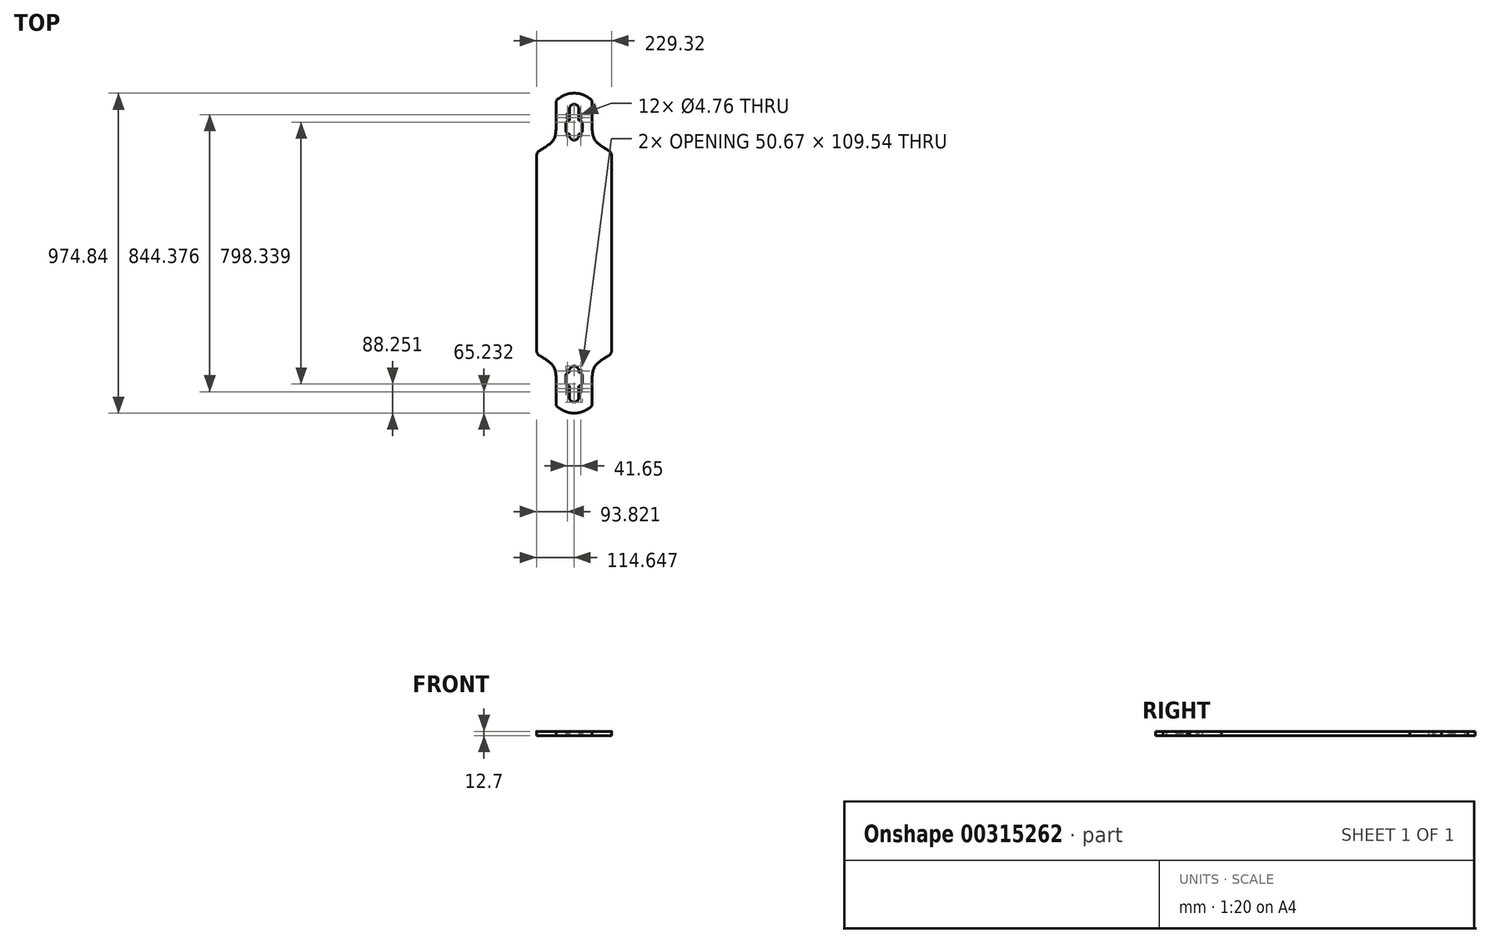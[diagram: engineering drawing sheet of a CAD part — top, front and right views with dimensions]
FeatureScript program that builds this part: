
annotation { "Feature Type Name" : "Feature", "Feature Type Description" : "" }
export const myFeature = defineFeature(function(context is Context, id is Id, definition is map)
    precondition{}
    {
        {
            var Q0;
            Q0=qCreatedBy(makeId("Top.planeOp"),FACE);
            var sketch = newSketch(context, id + "F0", { "sketchPlane" : qUnion([Q0])});
            skPoint(sketch, "E0", {"position": v(0, 0) * mm});
            skLineSegment(sketch, "E1.MirrorCS", {"start": v(-55, -394.15) * mm, "end": v(-55, -382.03) * mm});
            skPoint(sketch, "E2.MirrorCS.start.orphan", {"position": v(-55, -457.65) * mm});
            skFitSpline(sketch, "E3", {"points": [v(-91.05, -321.09) * mm, v(-61.23, -348.34) * mm, v(-55, -394.15) * mm], "startDerivative": vector(73.71, -48.62) * mm, "endDerivative": vector(-0.76, -96.96) * mm});
            skPoint(sketch, "E4.MirrorCS.start.orphan", {"position": v(-55, -344.7) * mm});
            skFitSpline(sketch, "E5.MirrorCS", {"points": [v(-91.05, 321.09) * mm, v(-61.23, 348.34) * mm, v(-55, 394.15) * mm], "startDerivative": vector(73.71, 48.62) * mm, "endDerivative": vector(-0.76, 96.96) * mm});
            skFitSpline(sketch, "E6.MirrorCS", {"points": [v(-114.62, 287.27) * mm, v(-112.13, 305.97) * mm, v(-91.05, 321.09) * mm], "startDerivative": vector(-0.84, 40.81) * mm, "endDerivative": vector(67.4, 45.38) * mm});
            skArc(sketch, "E7.MirrorCS", {"start": v(0, 478.34) * mm, "mid": v(0, 478.34) * mm, "end": v(0, 478.34) * mm});
            skFitSpline(sketch, "E8.MirrorCS", {"points": [v(91.05, 321.09) * mm, v(61.23, 348.34) * mm, v(55, 394.15) * mm], "startDerivative": vector(-73.71, 48.62) * mm, "endDerivative": vector(0.76, 96.96) * mm});
            skFitSpline(sketch, "E9.MirrorCS", {"points": [v(91.05, -321.09) * mm, v(61.23, -348.34) * mm, v(55, -394.15) * mm], "startDerivative": vector(-73.71, -48.62) * mm, "endDerivative": vector(0.76, -96.96) * mm});
            skLineSegment(sketch, "E10", {"start": v(-55, -394.15) * mm, "end": v(-55, -464.1) * mm});
            skPoint(sketch, "E11.startSnap0", {"position": v(0, 478.34) * mm});
            skArc(sketch, "E12", {"start": v(-55, -464.1) * mm, "mid": v(0, -487.42) * mm, "end": v(55, -464.1) * mm});
            skArc(sketch, "E13.MirrorCS", {"start": v(-55, 464.1) * mm, "mid": v(0, 487.42) * mm, "end": v(55, 464.12) * mm});
            skLineSegment(sketch, "E14", {"start": v(-55, 464.1) * mm, "end": v(-55, 394.15) * mm});
            skLineSegment(sketch, "E15", {"start": v(55, 464.12) * mm, "end": v(54.97, 370.51) * mm});
            skPoint(sketch, "E16.MirrorCS.start.orphan", {"position": v(55.02, -394.15) * mm});
            skLineSegment(sketch, "E17.trimOffspring", {"start": v(54.97, -383.98) * mm, "end": v(54.97, -394.15) * mm});
            skLineSegment(sketch, "E18.MirrorCS", {"start": v(55, -464.12) * mm, "end": v(54.97, -370.51) * mm});
            skFitSpline(sketch, "E19.MirrorCS", {"points": [v(91.05, -321.09) * mm, v(61.23, -348.34) * mm, v(55, -394.15) * mm], "startDerivative": vector(-73.71, -48.62) * mm, "endDerivative": vector(0.76, -96.96) * mm});
            skFitSpline(sketch, "E20.MirrorCS", {"points": [v(-114.62, -287.27) * mm, v(-112.13, -305.97) * mm, v(-91.05, -321.09) * mm], "startDerivative": vector(-0.84, -40.81) * mm, "endDerivative": vector(67.4, -45.38) * mm});
            skLineSegment(sketch, "E21", {"start": v(-114.62, 287.27) * mm, "end": v(-114.62, -287.27) * mm});
            skFitSpline(sketch, "E22.MirrorCS", {"points": [v(114.62, 287.27) * mm, v(112.13, 305.97) * mm, v(91.05, 321.09) * mm], "startDerivative": vector(0.84, 40.81) * mm, "endDerivative": vector(-67.4, 45.38) * mm});
            skFitSpline(sketch, "E23.MirrorCS", {"points": [v(114.62, -287.27) * mm, v(112.13, -305.97) * mm, v(91.05, -321.09) * mm], "startDerivative": vector(0.84, -40.81) * mm, "endDerivative": vector(-67.4, -45.38) * mm});
            skLineSegment(sketch, "E24.MirrorCS", {"start": v(114.62, 287.27) * mm, "end": v(114.62, -287.27) * mm});
            skPoint(sketch, "E25.startSnap0", {"position": v(2, 478.03) * mm});
            skCircle(sketch, "E26.MirrorC", {"center": v(-20.84, -422.19) * mm, "radius": 2.38 * mm});
            skLineSegment(sketch, "E27.MirrorCS", {"start": v(-14.3, -439.65) * mm, "end": v(-14.28, -422.19) * mm});
            skLineSegment(sketch, "E28.MirrorCS", {"start": v(-14.3, -439.65) * mm, "end": v(-14.26, -412.67) * mm});
            skLineSegment(sketch, "E29.MirrorCS", {"start": v(-14.19, -356.9) * mm, "end": v(-14.2, -363.24) * mm});
            skCircle(sketch, "E30.MirrorC", {"center": v(-20.84, -412.66) * mm, "radius": 2.38 * mm});
            skLineSegment(sketch, "E31.MirrorCS", {"start": v(14.16, -358.69) * mm, "end": v(14.27, -358.69) * mm});
            skCircle(sketch, "E32.MirrorC", {"center": v(-20.76, -358.69) * mm, "radius": 2.38 * mm});
            skLineSegment(sketch, "E33.MirrorCS", {"start": v(-25.32, -374.35) * mm, "end": v(-25.35, -393.39) * mm});
            skCircle(sketch, "E34.MirrorC", {"center": v(20.51, -358.69) * mm, "radius": 2.38 * mm});
            skArc(sketch, "E35.MirrorC", {"start": v(-14.25, -404.52) * mm, "mid": v(-22.1, -401.25) * mm, "end": v(-25.35, -393.39) * mm});
            skArc(sketch, "E36.MirrorC", {"start": v(-19.95, -383.87) * mm, "mid": v(-20.38, -383.6) * mm, "end": v(-20.8, -383.3) * mm});
            skCircle(sketch, "E37.MirrorC", {"center": v(20.81, -422.19) * mm, "radius": 2.38 * mm});
            skCircle(sketch, "E38.MirrorC", {"center": v(20.81, -412.66) * mm, "radius": 2.38 * mm});
            skLineSegment(sketch, "E39.MirrorCS", {"start": v(14.27, -439.65) * mm, "end": v(14.23, -404.52) * mm});
            skArc(sketch, "E40.MirrorC", {"start": v(14.27, -439.61) * mm, "mid": v(-0.01, -453.94) * mm, "end": v(-14.3, -439.61) * mm});
            skArc(sketch, "E41.MirrorC", {"start": v(14.23, -404.52) * mm, "mid": v(22.08, -401.25) * mm, "end": v(25.32, -393.39) * mm});
            skArc(sketch, "E42.MirrorC", {"start": v(14.17, -363.24) * mm, "mid": v(22.04, -366.49) * mm, "end": v(25.3, -374.35) * mm});
            skPoint(sketch, "E43.MirrorP", {"position": v(-10.33, -439.65) * mm});
            skArc(sketch, "E44.MirrorC", {"start": v(-14.2, -360.45) * mm, "mid": v(-0.01, -344.4) * mm, "end": v(14.17, -360.45) * mm});
            skLineSegment(sketch, "E45.trimOffspring", {"start": v(14.17, -363.24) * mm, "end": v(14.16, -356.9) * mm});
            skLineSegment(sketch, "E46.trimOffspring", {"start": v(-20.8, -383.3) * mm, "end": v(-20.8, -384.43) * mm});
            skArc(sketch, "E47.trimOffspring", {"start": v(-25.32, -374.35) * mm, "mid": v(-22.06, -366.49) * mm, "end": v(-14.2, -363.24) * mm});
            skArc(sketch, "E48.trimOffspring", {"start": v(-20.8, -384.43) * mm, "mid": v(-20.38, -384.14) * mm, "end": v(-19.95, -383.87) * mm});
            skLineSegment(sketch, "E49.trimOffspring", {"start": v(-14.2, -363.24) * mm, "end": v(-14.2, -360.45) * mm});
            skPoint(sketch, "E50.orphan", {"position": v(-14.24, -398.27) * mm});
            skLineSegment(sketch, "E51.trimOffspring", {"start": v(-14.19, -358.69) * mm, "end": v(-14.19, -356.9) * mm});
            skLineSegment(sketch, "E52.trimOffspring", {"start": v(14.27, -358.69) * mm, "end": v(14.16, -358.69) * mm});
            skLineSegment(sketch, "E53", {"start": v(-14.25, -404.52) * mm, "end": v(-14.26, -412.67) * mm});
            skLineSegment(sketch, "E54.MirrorCS", {"start": v(25.3, -374.35) * mm, "end": v(25.32, -393.39) * mm});
            skPoint(sketch, "E55.startSnap0", {"position": v(0, -487.42) * mm});
            skLineSegment(sketch, "E56", {"start": v(0, 0) * mm, "end": v(54.24, 0) * mm});
            skLineSegment(sketch, "E57.MirrorCS", {"start": v(14.16, 358.69) * mm, "end": v(14.27, 358.69) * mm});
            skLineSegment(sketch, "E58.MirrorCS", {"start": v(14.27, 358.69) * mm, "end": v(14.16, 358.69) * mm});
            skLineSegment(sketch, "E59.MirrorCS", {"start": v(14.17, 363.24) * mm, "end": v(14.16, 356.9) * mm});
            skLineSegment(sketch, "E60.MirrorCS", {"start": v(-20.8, 383.3) * mm, "end": v(-20.8, 384.43) * mm});
            skArc(sketch, "E61.MirrorCS", {"start": v(-20.8, 384.43) * mm, "mid": v(-20.38, 384.14) * mm, "end": v(-19.95, 383.87) * mm});
            skArc(sketch, "E62.MirrorCS", {"start": v(-19.95, 383.87) * mm, "mid": v(-20.38, 383.6) * mm, "end": v(-20.8, 383.3) * mm});
            skLineSegment(sketch, "E63.MirrorCS", {"start": v(-14.2, 363.24) * mm, "end": v(-14.2, 360.45) * mm});
            skLineSegment(sketch, "E64.MirrorCS", {"start": v(-14.19, 358.69) * mm, "end": v(-14.19, 356.9) * mm});
            skLineSegment(sketch, "E65.MirrorCS", {"start": v(-14.19, 356.9) * mm, "end": v(-14.2, 363.24) * mm});
            skLineSegment(sketch, "E66.MirrorCS", {"start": v(-14.25, 404.52) * mm, "end": v(-14.26, 412.67) * mm});
            skCircle(sketch, "E67.MirrorC", {"center": v(20.81, 412.66) * mm, "radius": 2.38 * mm});
            skCircle(sketch, "E68.MirrorC", {"center": v(20.51, 358.69) * mm, "radius": 2.38 * mm});
            skLineSegment(sketch, "E69.MirrorCS", {"start": v(-14.3, 439.65) * mm, "end": v(-14.28, 422.19) * mm});
            skCircle(sketch, "E70.MirrorC", {"center": v(-20.84, 412.66) * mm, "radius": 2.38 * mm});
            skCircle(sketch, "E71.MirrorC", {"center": v(-20.84, 422.19) * mm, "radius": 2.38 * mm});
            skCircle(sketch, "E72.MirrorC", {"center": v(20.81, 422.19) * mm, "radius": 2.38 * mm});
            skCircle(sketch, "E73.MirrorC", {"center": v(-20.76, 358.69) * mm, "radius": 2.38 * mm});
            skPoint(sketch, "E74.MirrorP", {"position": v(-14.24, 398.27) * mm});
            skArc(sketch, "E75.MirrorCS", {"start": v(-14.25, 404.52) * mm, "mid": v(-22.1, 401.25) * mm, "end": v(-25.35, 393.39) * mm});
            skArc(sketch, "E76.MirrorCS", {"start": v(14.23, 404.52) * mm, "mid": v(22.08, 401.25) * mm, "end": v(25.32, 393.39) * mm});
            skLineSegment(sketch, "E77.MirrorCS", {"start": v(-25.32, 374.35) * mm, "end": v(-25.35, 393.39) * mm});
            skPoint(sketch, "E78.MirrorP", {"position": v(-10.33, 439.65) * mm});
            skLineSegment(sketch, "E79.MirrorCS", {"start": v(14.27, 439.65) * mm, "end": v(14.23, 404.52) * mm});
            skArc(sketch, "E80.MirrorCS", {"start": v(-14.2, 360.45) * mm, "mid": v(-0.01, 344.4) * mm, "end": v(14.17, 360.45) * mm});
            skLineSegment(sketch, "E81.MirrorCS", {"start": v(-14.3, 439.65) * mm, "end": v(-14.26, 412.67) * mm});
            skArc(sketch, "E82.MirrorCS", {"start": v(14.17, 363.24) * mm, "mid": v(22.04, 366.49) * mm, "end": v(25.3, 374.35) * mm});
            skArc(sketch, "E83.MirrorCS", {"start": v(-25.32, 374.35) * mm, "mid": v(-22.06, 366.49) * mm, "end": v(-14.2, 363.24) * mm});
            skLineSegment(sketch, "E84.MirrorCS", {"start": v(25.3, 374.35) * mm, "end": v(25.32, 393.39) * mm});
            skArc(sketch, "E85.MirrorCS", {"start": v(14.27, 439.61) * mm, "mid": v(-0.01, 453.94) * mm, "end": v(-14.3, 439.61) * mm});
            skSolve(sketch);
        }
        {
            var Q0;
            Q0 = qSketchRegion(id + "F0", true);
            extrude(context, id + "F1", {"entities" : qUnion([Q0]), "depth" : 12.7 * mm, "offsetDistance" : 25.4 * mm});
        }
    });
